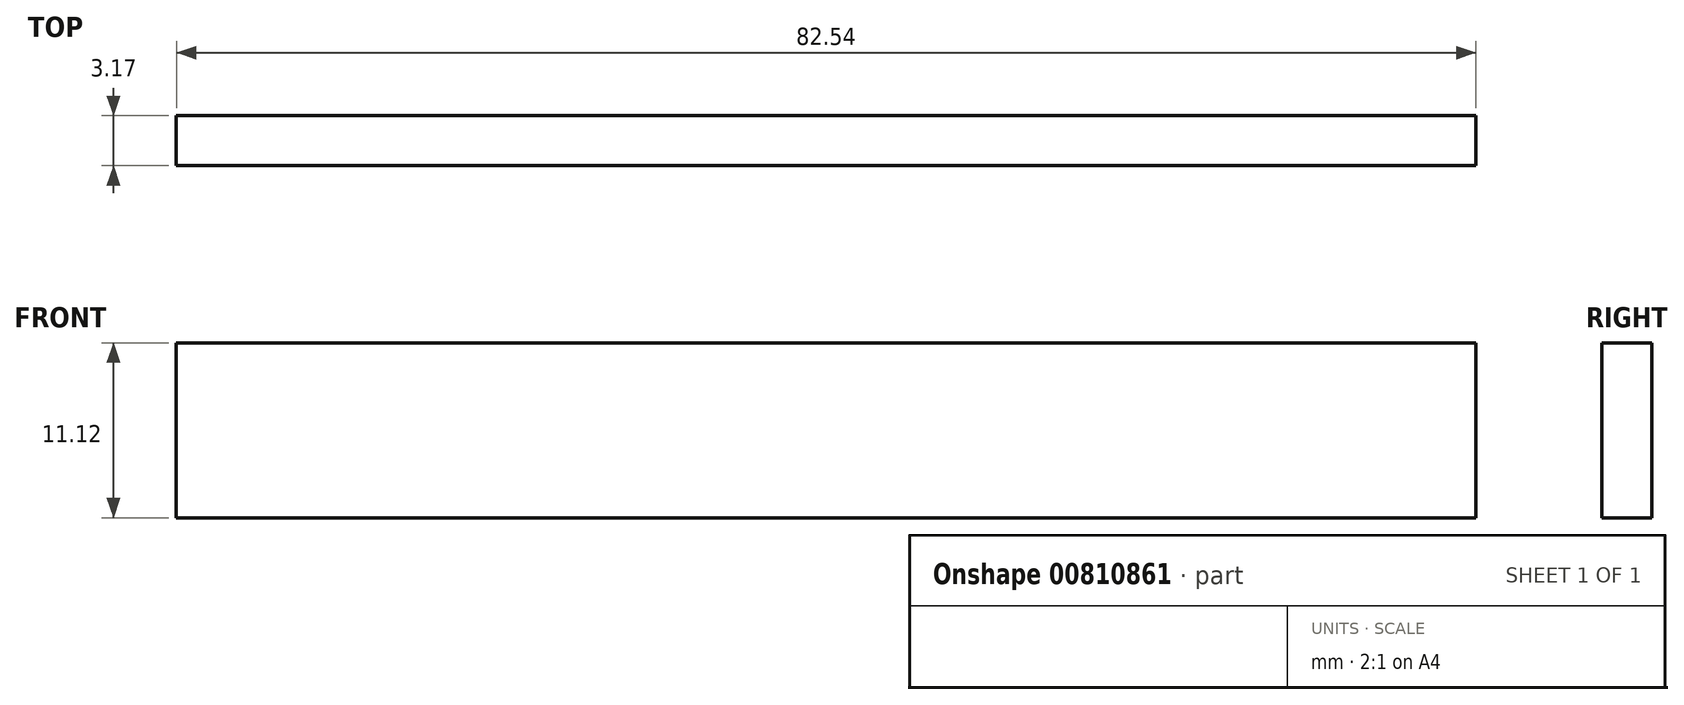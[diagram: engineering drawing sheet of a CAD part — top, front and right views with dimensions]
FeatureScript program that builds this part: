
annotation { "Feature Type Name" : "Feature", "Feature Type Description" : "" }
export const myFeature = defineFeature(function(context is Context, id is Id, definition is map)
    precondition{}
    {
        {
            var Q0;
            Q0=qCreatedBy(makeId("Front.planeOp"),FACE);
            var sketch = newSketch(context, id + "F0", { "sketchPlane" : qUnion([Q0])});
            skLineSegment(sketch, "E0.bottom", {"start": v(41.28, 5.56) * mm, "end": v(-41.28, 5.56) * mm});
            skLineSegment(sketch, "E0.top", {"start": v(41.28, -5.56) * mm, "end": v(-41.28, -5.56) * mm});
            skLineSegment(sketch, "E0.left", {"start": v(41.28, 5.56) * mm, "end": v(41.28, -5.56) * mm});
            skLineSegment(sketch, "E0.right", {"start": v(-41.28, 5.56) * mm, "end": v(-41.28, -5.56) * mm});
            skPoint(sketch, "E0.middle", {"position": v(0, 0) * mm});
            skSolve(sketch);
        }
        {
            var Q0;
            Q0=makeQuery(id+"F0.imprint","IMPRINT",FACE,{"disambiguationData":[TD([[makeQuery(id+"F0.imprint","IMPRINT",EDGE,{"derivedFrom":sQuery(id+"F0.wireOp",EDGE,"E0.bottom")}),1.0]])]});
            extrude(context, id + "F1", {"entities" : qUnion([Q0]), "depth" : 3.17 * mm, "offsetDistance" : 25.4 * mm});
        }
    });
